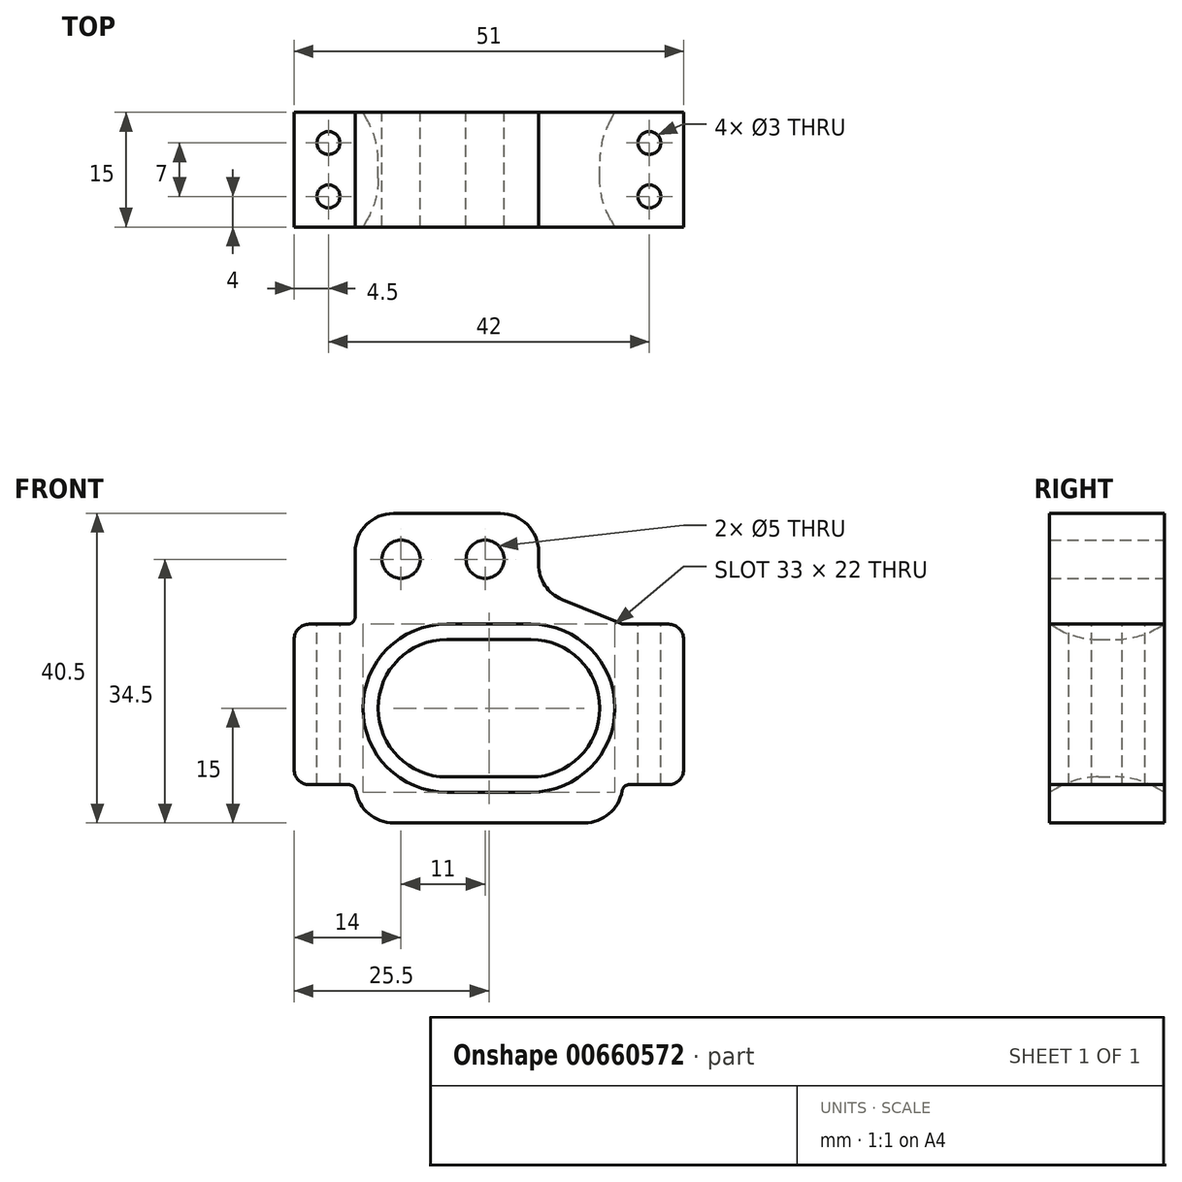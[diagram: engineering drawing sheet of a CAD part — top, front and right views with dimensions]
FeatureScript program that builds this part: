
annotation { "Feature Type Name" : "Feature", "Feature Type Description" : "" }
export const myFeature = defineFeature(function(context is Context, id is Id, definition is map)
    precondition{}
    {
        {
            var Q0;
            Q0=qCreatedBy(makeId("Front.planeOp"),FACE);
            var sketch = newSketch(context, id + "F0", { "sketchPlane" : qUnion([Q0])});
            skArc(sketch, "E0", {"start": v(0, 9) * mm, "mid": v(-9, 0) * mm, "end": v(0, -9) * mm});
            skArc(sketch, "E1", {"start": v(11, -9) * mm, "mid": v(20, 0) * mm, "end": v(11, 9) * mm});
            skLineSegment(sketch, "E2", {"start": v(0, 9) * mm, "end": v(11, 9) * mm});
            skLineSegment(sketch, "E3", {"start": v(0, -9) * mm, "end": v(11, -9) * mm});
            skLineSegment(sketch, "E4", {"start": v(21.52, -9) * mm, "end": v(21.9, -8.8) * mm});
            skPoint(sketch, "E5.orphan", {"position": v(21.52, 9) * mm});
            skCircle(sketch, "E6", {"center": v(-6, 19.5) * mm, "radius": 2.5 * mm});
            skCircle(sketch, "E7", {"center": v(5, 19.5) * mm, "radius": 2.5 * mm});
            skLineSegment(sketch, "E8", {"start": v(-20, 0) * mm, "end": v(-20, 11) * mm});
            skLineSegment(sketch, "E9", {"start": v(-12, 25.5) * mm, "end": v(12, 25.5) * mm});
            skLineSegment(sketch, "E10", {"start": v(31, 11) * mm, "end": v(31, -10) * mm});
            skLineSegment(sketch, "E11", {"start": v(23, -15) * mm, "end": v(-12, -15) * mm});
            skLineSegment(sketch, "E12", {"start": v(-20, -15) * mm, "end": v(-20.65, -14.78) * mm});
            skLineSegment(sketch, "E13", {"start": v(-20, -10) * mm, "end": v(-20, 0) * mm});
            skLineSegment(sketch, "E14", {"start": v(-12, 25.5) * mm, "end": v(-12, 11) * mm});
            skLineSegment(sketch, "E15", {"start": v(-12, 11) * mm, "end": v(-20, 11) * mm});
            skLineSegment(sketch, "E16", {"start": v(-20, -10) * mm, "end": v(-12, -10) * mm});
            skLineSegment(sketch, "E17", {"start": v(-12, -10) * mm, "end": v(-12, -15) * mm});
            skLineSegment(sketch, "E18", {"start": v(23, 11) * mm, "end": v(31, 11) * mm});
            skLineSegment(sketch, "E19", {"start": v(31, -10) * mm, "end": v(23, -10) * mm});
            skLineSegment(sketch, "E20", {"start": v(23, -10) * mm, "end": v(23, -15) * mm});
            skPoint(sketch, "E21.orphan", {"position": v(23, 25.5) * mm});
            skLineSegment(sketch, "E22", {"start": v(12, 25.5) * mm, "end": v(12, 15.5) * mm});
            skLineSegment(sketch, "E23", {"start": v(23, 11) * mm, "end": v(12, 15.5) * mm});
            skPoint(sketch, "E24.end.orphan", {"position": v(23, 15.5) * mm});
            skSolve(sketch);
        }
        {
            var Q0;
            Q0=makeQuery(id+"F0.imprint","IMPRINT",FACE,{"disambiguationData":[TD([[makeQuery(id+"F0.imprint","IMPRINT",EDGE,{"derivedFrom":sQuery(id+"F0.wireOp",EDGE,"E0")}),-1.0]])]});
            extrude(context, id + "F1", {"entities" : qUnion([Q0]), "depth" : 15 * mm, "offsetDistance" : 25 * mm});
        }
        {
            var Q0;
            Q0=makeQuery(id+"F1.opExtrude","SWEPT_EDGE",EDGE,{"disambiguationData":[OSD([sQuery(id+"F0.wireOp",EDGE,"E9"),sQuery(id+"F0.wireOp",EDGE,"E22")])]});
            var Q1;
            Q1=makeQuery(id+"F1.opExtrude","SWEPT_EDGE",EDGE,{"disambiguationData":[OSD([sQuery(id+"F0.wireOp",EDGE,"E9"),sQuery(id+"F0.wireOp",EDGE,"E14")])]});
            var Q2;
            Q2=makeQuery(id+"F1.opExtrude","SWEPT_EDGE",EDGE,{"disambiguationData":[OSD([sQuery(id+"F0.wireOp",EDGE,"E11"),sQuery(id+"F0.wireOp",EDGE,"E17")])]});
            var Q3;
            Q3=makeQuery(id+"F1.opExtrude","SWEPT_EDGE",EDGE,{"disambiguationData":[OSD([sQuery(id+"F0.wireOp",EDGE,"E11"),sQuery(id+"F0.wireOp",EDGE,"E20")])]});
            var Q4;
            Q4=makeQuery(id+"F1.opExtrude","SWEPT_EDGE",EDGE,{"disambiguationData":[OSD([sQuery(id+"F0.wireOp",EDGE,"E22"),sQuery(id+"F0.wireOp",EDGE,"E23")])]});
            fillet(context, id + "F2", {"entities" : qUnion([Q0, Q1, Q2, Q3, Q4]), "radius" : 5 * mm, "tangentPropagation" : true, "allowEdgeOverflow" : false});
        }
        {
            var Q0;
            Q0=makeQuery(id+"F1.opExtrude","SWEPT_FACE",FACE,{"disambiguationData":[OSD([sQuery(id+"F0.wireOp",EDGE,"E15")])]});
            var sketch = newSketch(context, id + "F3", { "sketchPlane" : qUnion([Q0])});
            skLineSegment(sketch, "E25", {"start": v(-15.5, 0) * mm, "end": v(-15.5, -15) * mm, "construction": true});
            skCircle(sketch, "E26", {"center": v(-15.5, -4) * mm, "radius": 1.5 * mm});
            skCircle(sketch, "E27", {"center": v(-15.5, -11) * mm, "radius": 1.5 * mm});
            skSolve(sketch);
        }
        {
            var Q0;
            Q0=makeQuery(id+"F3.imprint","IMPRINT",FACE,{"disambiguationData":[TD([[makeQuery(id+"F3.imprint","IMPRINT",EDGE,{"derivedFrom":sQuery(id+"F3.wireOp",EDGE,"E26")}),1.0]])]});
            var Q1;
            Q1=makeQuery(id+"F3.imprint","IMPRINT",FACE,{"disambiguationData":[TD([[makeQuery(id+"F3.imprint","IMPRINT",EDGE,{"derivedFrom":sQuery(id+"F3.wireOp",EDGE,"E27")}),1.0]])]});
            extrude(context, id + "F4", {"entities" : qUnion([Q0, Q1]), "operationType" : NewBodyOperationType.REMOVE, "oppositeDirection" : true, "depth" : 25 * mm, "offsetDistance" : 25 * mm});
        }
        {
            var Q0;
            Q0=makeQuery(id+"F1.opExtrude","SWEPT_FACE",FACE,{"disambiguationData":[OSD([sQuery(id+"F0.wireOp",EDGE,"E18")])]});
            var sketch = newSketch(context, id + "F5", { "sketchPlane" : qUnion([Q0])});
            skLineSegment(sketch, "E28", {"start": v(26.5, 0) * mm, "end": v(26.5, -15) * mm, "construction": true});
            skCircle(sketch, "E29", {"center": v(26.5, -4) * mm, "radius": 1.5 * mm});
            skCircle(sketch, "E30", {"center": v(26.5, -11) * mm, "radius": 1.5 * mm});
            skSolve(sketch);
        }
        {
            var Q0;
            Q0=makeQuery(id+"F5.imprint","IMPRINT",FACE,{"disambiguationData":[TD([[makeQuery(id+"F5.imprint","IMPRINT",EDGE,{"derivedFrom":sQuery(id+"F5.wireOp",EDGE,"E29")}),1.0]])]});
            var Q1;
            Q1=makeQuery(id+"F5.imprint","IMPRINT",FACE,{"disambiguationData":[TD([[makeQuery(id+"F5.imprint","IMPRINT",EDGE,{"derivedFrom":sQuery(id+"F5.wireOp",EDGE,"E30")}),1.0]])]});
            extrude(context, id + "F6", {"entities" : qUnion([Q0, Q1]), "operationType" : NewBodyOperationType.REMOVE, "oppositeDirection" : true, "depth" : 25 * mm, "offsetDistance" : 25 * mm});
        }
        {
            var Q0;
            Q0=makeQuery(id+"F1.opExtrude","CAP_EDGE",EDGE,{"disambiguationData":[OSD([sQuery(id+"F0.wireOp",EDGE,"E0")])],"isStart":true});
            var Q1;
            Q1=makeQuery(id+"F1.opExtrude","CAP_EDGE",EDGE,{"disambiguationData":[OSD([sQuery(id+"F0.wireOp",EDGE,"E2")])],"isStart":true});
            var Q2;
            Q2=makeQuery(id+"F1.opExtrude","CAP_EDGE",EDGE,{"disambiguationData":[OSD([sQuery(id+"F0.wireOp",EDGE,"E2")])],"isStart":false});
            chamfer(context, id + "F7", {"entities" : qUnion([Q0, Q1, Q2]), "chamferType" : ChamferType.OFFSET_ANGLE, "width" : 2 * mm, "oppositeDirection" : false, "angle" : 60 * degree, "tangentPropagation" : true});
        }
        {
            var Q0;
            {var subQ0=sQuery(id+"F0.wireOp",EDGE,"E0");Q0=makeQuery(id+"F7.opChamfer","BLEND_EDGE",EDGE,{"blendedFrom":[makeQuery(id+"F1.opExtrude","CAP_EDGE",EDGE,{"disambiguationData":[OSD([subQ0])],"isStart":false}),makeQuery(id+"F1.opExtrude","SWEPT_FACE",FACE,{"disambiguationData":[OSD([subQ0])]})],"blendedInto":[makeQuery(id+"F1.opExtrude","SWEPT_FACE",FACE,{"disambiguationData":[OSD([subQ0])]})]});}
            var Q1;
            {var subQ0=sQuery(id+"F0.wireOp",EDGE,"E0");Q1=makeQuery(id+"F7.opChamfer","BLEND_EDGE",EDGE,{"blendedFrom":[makeQuery(id+"F1.opExtrude","CAP_EDGE",EDGE,{"disambiguationData":[OSD([subQ0])],"isStart":true}),makeQuery(id+"F1.opExtrude","SWEPT_FACE",FACE,{"disambiguationData":[OSD([subQ0])]})],"blendedInto":[makeQuery(id+"F1.opExtrude","SWEPT_FACE",FACE,{"disambiguationData":[OSD([subQ0])]})]});}
            fillet(context, id + "F8", {"entities" : qUnion([Q0, Q1]), "radius" : 11 * mm, "tangentPropagation" : true, "allowEdgeOverflow" : false});
        }
        {
            var Q0;
            Q0=makeQuery(id+"F1.opExtrude","SWEPT_EDGE",EDGE,{"disambiguationData":[OSD([sQuery(id+"F0.wireOp",EDGE,"E8"),sQuery(id+"F0.wireOp",EDGE,"E15")])]});
            var Q1;
            Q1=makeQuery(id+"F1.opExtrude","SWEPT_EDGE",EDGE,{"disambiguationData":[OSD([sQuery(id+"F0.wireOp",EDGE,"E10"),sQuery(id+"F0.wireOp",EDGE,"E18")])]});
            var Q2;
            Q2=makeQuery(id+"F1.opExtrude","SWEPT_EDGE",EDGE,{"disambiguationData":[OSD([sQuery(id+"F0.wireOp",EDGE,"E10"),sQuery(id+"F0.wireOp",EDGE,"E19")])]});
            var Q3;
            Q3=makeQuery(id+"F1.opExtrude","SWEPT_EDGE",EDGE,{"disambiguationData":[OSD([sQuery(id+"F0.wireOp",EDGE,"E13"),sQuery(id+"F0.wireOp",EDGE,"E16")])]});
            fillet(context, id + "F9", {"entities" : qUnion([Q0, Q1, Q2, Q3]), "radius" : 2 * mm, "tangentPropagation" : true, "allowEdgeOverflow" : false});
        }
        {
            var Q0;
            Q0=makeQuery(id+"F1.opExtrude","SWEPT_EDGE",EDGE,{"disambiguationData":[OSD([sQuery(id+"F0.wireOp",EDGE,"E14"),sQuery(id+"F0.wireOp",EDGE,"E15")])]});
            var Q1;
            Q1=makeQuery(id+"F1.opExtrude","SWEPT_EDGE",EDGE,{"disambiguationData":[OSD([sQuery(id+"F0.wireOp",EDGE,"E18"),sQuery(id+"F0.wireOp",EDGE,"E23")])]});
            var Q2;
            Q2=makeQuery(id+"F2.opFillet","BLEND_EDGE",EDGE,{"blendedFrom":[makeQuery(id+"F1.opExtrude","SWEPT_EDGE",EDGE,{"disambiguationData":[OSD([sQuery(id+"F0.wireOp",EDGE,"E11"),sQuery(id+"F0.wireOp",EDGE,"E20")])]}),makeQuery(id+"F1.opExtrude","SWEPT_FACE",FACE,{"disambiguationData":[OSD([sQuery(id+"F0.wireOp",EDGE,"E19")])]})],"blendedInto":[makeQuery(id+"F1.opExtrude","SWEPT_FACE",FACE,{"disambiguationData":[OSD([sQuery(id+"F0.wireOp",EDGE,"E19")])]})]});
            var Q3;
            Q3=makeQuery(id+"F2.opFillet","BLEND_EDGE",EDGE,{"blendedFrom":[makeQuery(id+"F1.opExtrude","SWEPT_EDGE",EDGE,{"disambiguationData":[OSD([sQuery(id+"F0.wireOp",EDGE,"E11"),sQuery(id+"F0.wireOp",EDGE,"E17")])]}),makeQuery(id+"F1.opExtrude","SWEPT_FACE",FACE,{"disambiguationData":[OSD([sQuery(id+"F0.wireOp",EDGE,"E16")])]})],"blendedInto":[makeQuery(id+"F1.opExtrude","SWEPT_FACE",FACE,{"disambiguationData":[OSD([sQuery(id+"F0.wireOp",EDGE,"E16")])]})]});
            fillet(context, id + "F10", {"entities" : qUnion([Q0, Q1, Q2, Q3]), "radius" : 1 * mm, "tangentPropagation" : true, "allowEdgeOverflow" : false});
        }
    });
